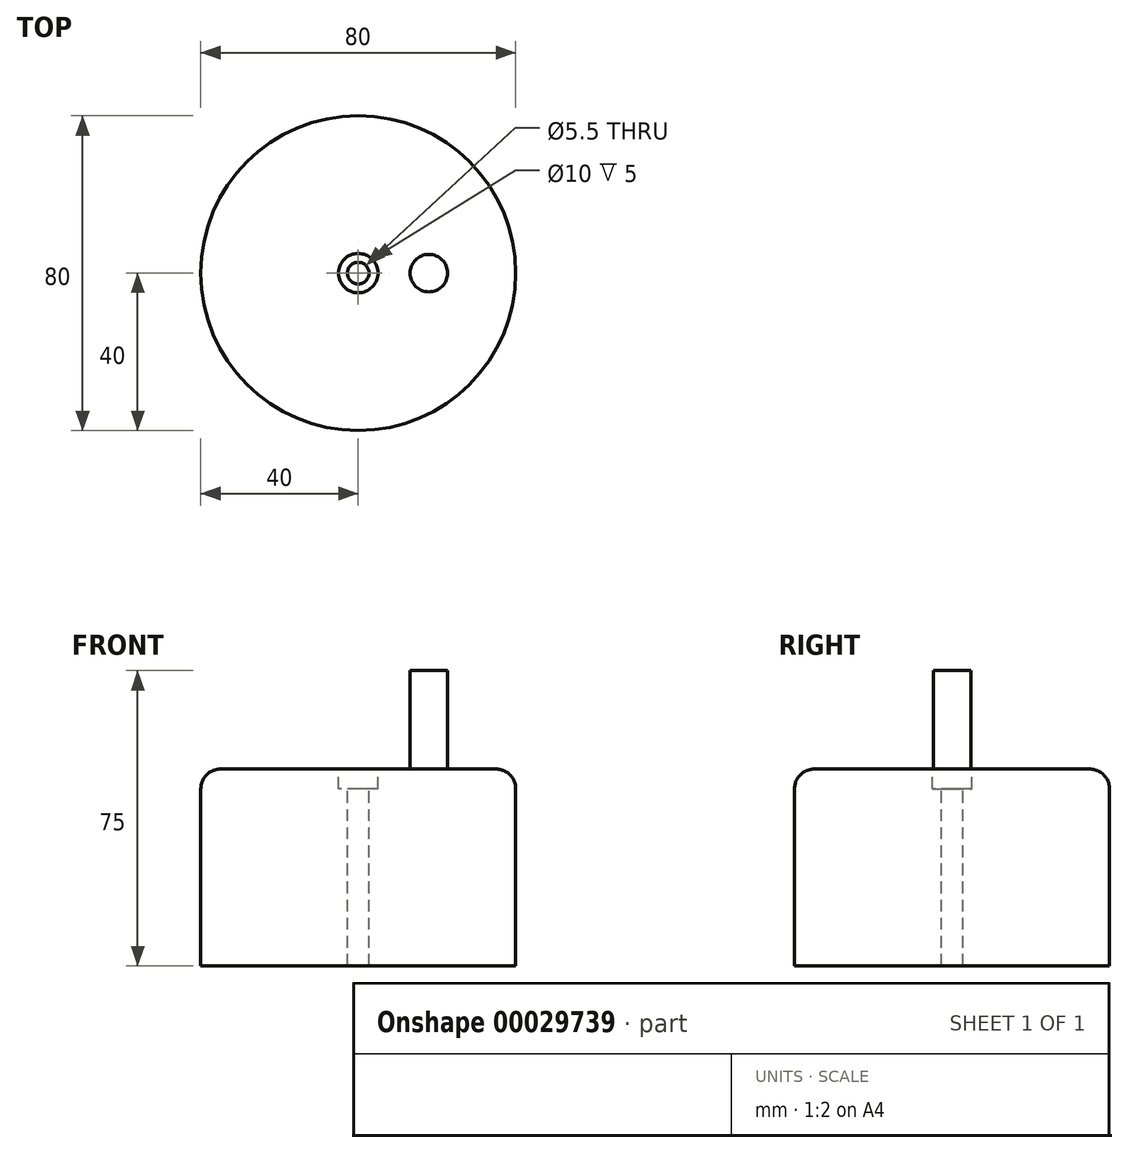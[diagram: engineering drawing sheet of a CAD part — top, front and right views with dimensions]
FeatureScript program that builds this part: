
annotation { "Feature Type Name" : "Feature", "Feature Type Description" : "" }
export const myFeature = defineFeature(function(context is Context, id is Id, definition is map)
    precondition{}
    {
        {
            var Q0;
            Q0=qCreatedBy(makeId("Front.planeOp"),FACE);
            var sketch = newSketch(context, id + "F0", { "sketchPlane" : qUnion([Q0])});
            skLineSegment(sketch, "E0.bottom", {"start": v(0, 0) * mm, "end": v(40, 0) * mm});
            skLineSegment(sketch, "E0.top", {"start": v(0, 50) * mm, "end": v(40, 50) * mm});
            skLineSegment(sketch, "E0.left", {"start": v(0, 0) * mm, "end": v(0, 50) * mm});
            skLineSegment(sketch, "E0.right", {"start": v(40, 0) * mm, "end": v(40, 50) * mm});
            skSolve(sketch);
        }
        {
            var Q0;
            Q0=makeQuery(id+"F0.imprint","IMPRINT",FACE,{"disambiguationData":[TD([[makeQuery(id+"F0.imprint","IMPRINT",EDGE,{"derivedFrom":sQuery(id+"F0.wireOp",EDGE,"E0.bottom")}),1.0]])]});
            var Q1;
            Q1=sQuery(id+"F0.wireOp",EDGE,"E0.left");
            revolve(context, id + "F1", {"entities" : qUnion([Q0]), "axis" : qUnion([Q1]), "revolveType" : RevolveType.FULL});
        }
        {
            var Q0;
            Q0=makeQuery(id+"F1.opRevolve","SWEPT_FACE",FACE,{"disambiguationData":[OSD([sQuery(id+"F0.wireOp",EDGE,"E0.top")])]});
            var sketch = newSketch(context, id + "F2", { "sketchPlane" : qUnion([Q0])});
            skPoint(sketch, "E1", {"position": v(0, 0) * mm});
            skSolve(sketch);
        }
        {
            var Q0;
            Q0=sQuery(id+"F2.wireOp",VERTEX,"E1");
            var Q1;
            Q1=makeQuery(id+"F1.opRevolve","SWEPT_BODY",BODY,{"disambiguationData":[OSD([sQuery(id+"F0.wireOp",EDGE,"E0.bottom"),sQuery(id+"F0.wireOp",EDGE,"E0.top"),sQuery(id+"F0.wireOp",EDGE,"E0.left"),sQuery(id+"F0.wireOp",EDGE,"E0.right")])]});
            hole(context, id + "F3", {"style" : HoleStyle.C_BORE, "holeDiameter" : 5.5 * mm, "cBoreDiameter" : 10 * mm, "cBoreDepth" : 5 * mm, "endStyle" : HoleEndStyle.THROUGH, "locations" : qUnion([Q0]), "scope" : qUnion([Q1])});
        }
        {
            var Q0;
            Q0=makeQuery(id+"F1.opRevolve","SWEPT_EDGE",EDGE,{"disambiguationData":[OSD([sQuery(id+"F0.wireOp",EDGE,"E0.top"),sQuery(id+"F0.wireOp",EDGE,"E0.right")])]});
            fillet(context, id + "F4", {"entities" : qUnion([Q0]), "radius" : 5 * mm, "tangentPropagation" : true, "allowEdgeOverflow" : false});
        }
        {
            var Q0;
            Q0=makeQuery(id+"F1.opRevolve","SWEPT_FACE",FACE,{"disambiguationData":[OSD([sQuery(id+"F0.wireOp",EDGE,"E0.top")])]});
            var sketch = newSketch(context, id + "F5", { "sketchPlane" : qUnion([Q0])});
            skCircle(sketch, "E2", {"center": v(17.94, 0) * mm, "radius": 4.76 * mm});
            skSolve(sketch);
        }
        {
            var Q0;
            Q0=makeQuery(id+"F5.imprint","IMPRINT",FACE,{"disambiguationData":[TD([[makeQuery(id+"F5.imprint","IMPRINT",EDGE,{"derivedFrom":sQuery(id+"F5.wireOp",EDGE,"E2")}),1.0]])]});
            extrude(context, id + "F6", {"entities" : qUnion([Q0]), "operationType" : NewBodyOperationType.ADD, "depth" : 25 * mm});
        }
    });
